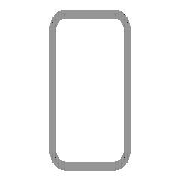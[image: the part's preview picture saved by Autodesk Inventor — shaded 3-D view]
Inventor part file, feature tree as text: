
AUTODESK INVENTOR PART (.ipt)
format: ipt  version: 2025.3 (Build 293356000, 356)  size: 148,992 bytes
history: native  units: mm (DEFAULTED — no unit token found)
features: other x4, plane x3, split x2, sketch x1
ambient origin geometry x8: Origin, YZ Plane, XZ Plane, XY Plane, X Axis, Y Axis, Z Axis, Center Point
bodies: Solid1 (feature_tree), Body (feature_tree)
feature tree (10):
  parser-record x1  (decoder bookkeeping rows leaked as tree rows — omitted from the tree; the rows remain in map.json)
  other  "Driven Length"
  other  "Start Plane"
  other  "End Plane"
  plane  "Work Plane4"
  split  "Split1"
  plane  "Work Plane5"
  split  "Split2"
  sketch  "Sketch3"  dims[d3=2701.920698mm d4=0.0mm d7=4.0mm d9=20.0mm d11=40.0mm d12=2.0mm d13=126.334848mm d14=2828.255546mm d15=10.0mm d16=20.0mm d17=90.0deg d18=2701.920698mm]
  plane  "Work Plane3"
